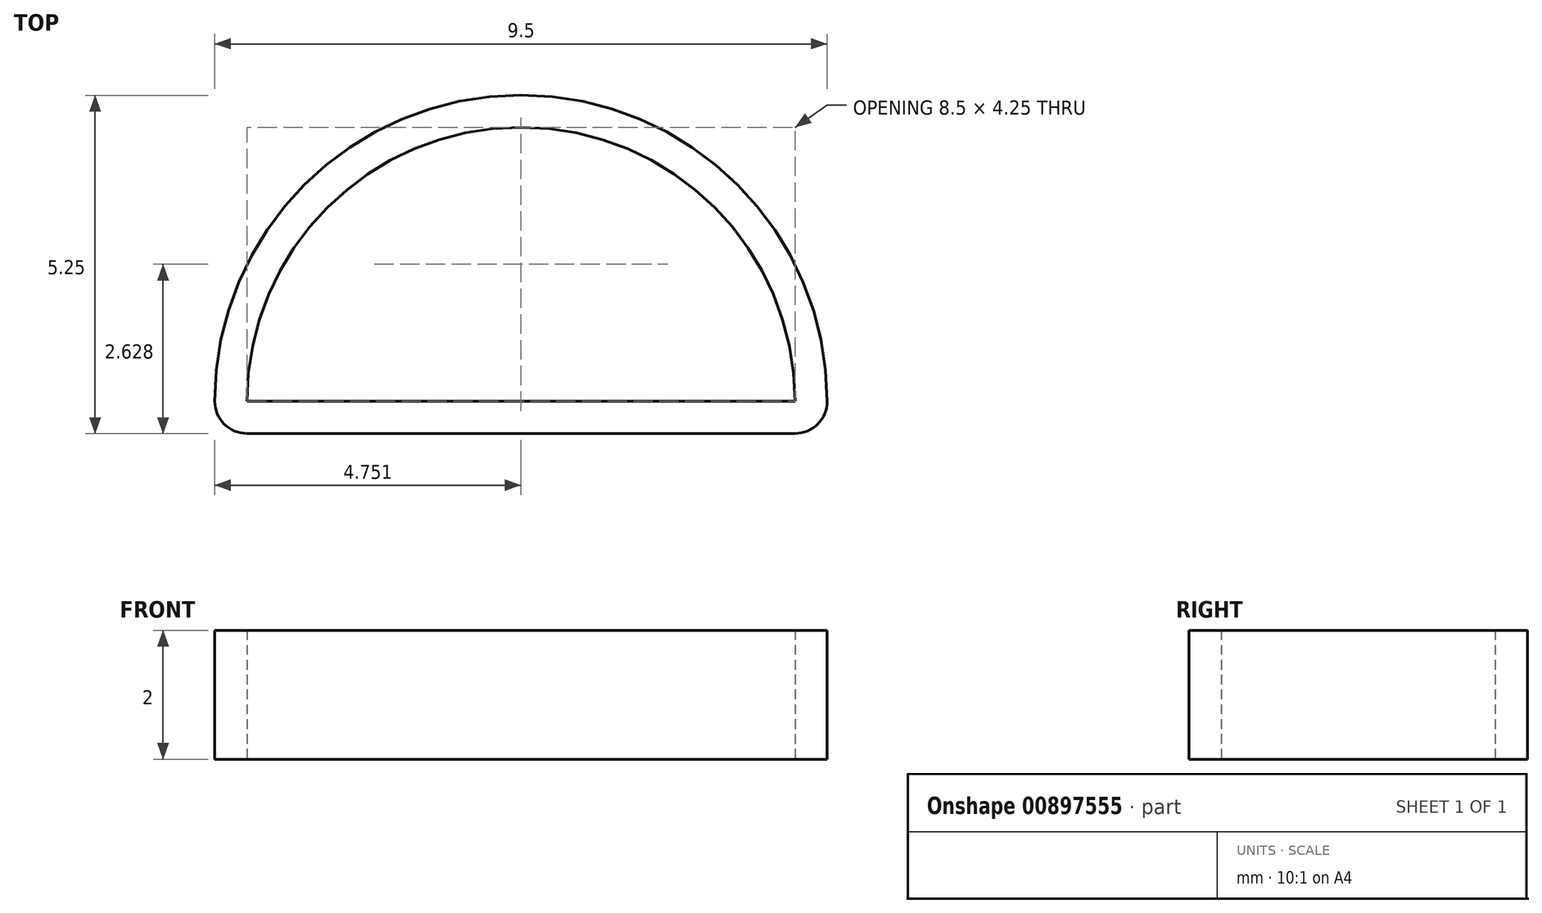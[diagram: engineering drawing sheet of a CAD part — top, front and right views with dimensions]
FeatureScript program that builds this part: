
annotation { "Feature Type Name" : "Feature", "Feature Type Description" : "" }
export const myFeature = defineFeature(function(context is Context, id is Id, definition is map)
    precondition{}
    {
        {
            var Q0;
            Q0=qCreatedBy(makeId("Top.planeOp"),FACE);
            var sketch = newSketch(context, id + "F0", { "sketchPlane" : qUnion([Q0])});
            skArc(sketch, "E0", {"start": v(-43.03, 39.33) * mm, "mid": v(-47.28, 43.58) * mm, "end": v(-51.53, 39.33) * mm});
            skLineSegment(sketch, "E1", {"start": v(-51.53, 39.33) * mm, "end": v(-43.03, 39.33) * mm});
            skLineSegment(sketch, "E2.0", {"start": v(-52, 38.83) * mm, "end": v(-42.56, 38.83) * mm});
            skArc(sketch, "E2.1", {"start": v(-42.56, 38.83) * mm, "mid": v(-47.28, 44.08) * mm, "end": v(-52, 38.83) * mm});
            skSolve(sketch);
        }
        {
            var Q0;
            Q0 = qSketchRegion(id + "F0", true);
            extrude(context, id + "F1", {"entities" : qUnion([Q0]), "depth" : 2 * mm, "offsetDistance" : 25 * mm});
        }
        {
            var Q0;
            {var subQ0=sQuery(id+"F0.wireOp",EDGE,"E2.1");var subQ1=sQuery(id+"F0.wireOp",EDGE,"E2.0");Q0=makeQuery(id+"F1.opExtrude","SWEPT_EDGE",EDGE,{"disambiguationData":[OSD([subQ1,subQ0]),TDD([makeQuery(id+"F0.imprint","INTERSECT",VERTEX,{"disambiguationData":[OD(0.0)],"derivedFrom":[subQ1,subQ0]})])]});}
            var Q1;
            {var subQ0=sQuery(id+"F0.wireOp",EDGE,"E2.1");var subQ1=sQuery(id+"F0.wireOp",EDGE,"E2.0");Q1=makeQuery(id+"F1.opExtrude","SWEPT_EDGE",EDGE,{"disambiguationData":[OSD([subQ1,subQ0]),TDD([makeQuery(id+"F0.imprint","INTERSECT",VERTEX,{"disambiguationData":[OD(1.0)],"derivedFrom":[subQ1,subQ0]})])]});}
            fillet(context, id + "F2", {"entities" : qUnion([Q0, Q1]), "radius" : 0.5 * mm, "tangentPropagation" : true, "allowEdgeOverflow" : false});
        }
    });
